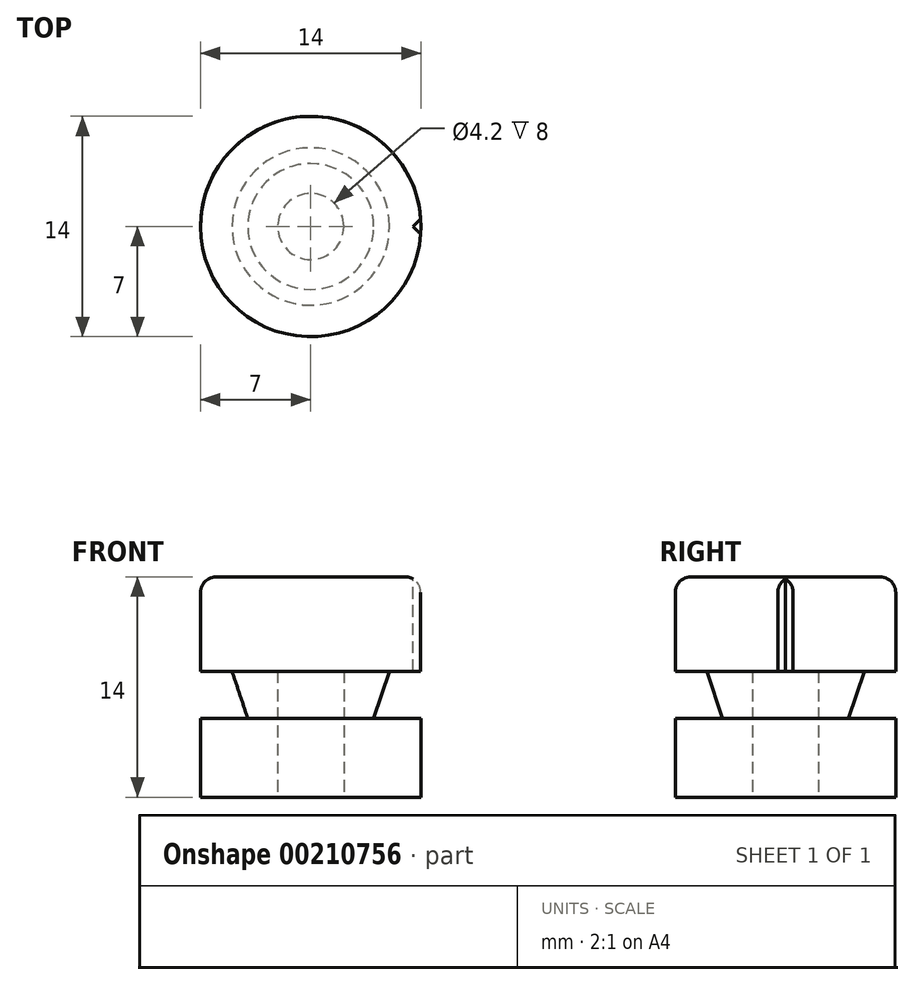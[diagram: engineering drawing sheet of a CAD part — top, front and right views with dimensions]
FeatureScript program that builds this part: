
annotation { "Feature Type Name" : "Feature", "Feature Type Description" : "" }
export const myFeature = defineFeature(function(context is Context, id is Id, definition is map)
    precondition{}
    {
        {
            var Q0;
            Q0=qCreatedBy(makeId("Top.planeOp"),FACE);
            var sketch = newSketch(context, id + "F0", { "sketchPlane" : qUnion([Q0])});
            skCircle(sketch, "E0", {"center": v(0, 0) * mm, "radius": 7 * mm});
            skSolve(sketch);
        }
        {
            var Q0;
            Q0 = qSketchRegion(id + "F0", true);
            extrude(context, id + "F1", {"entities" : qUnion([Q0]), "depth" : 14 * mm});
        }
        {
            var Q0;
            Q0=qCreatedBy(makeId("Front.planeOp"),FACE);
            var sketch = newSketch(context, id + "F2", { "sketchPlane" : qUnion([Q0])});
            skLineSegment(sketch, "E1", {"start": v(7, 8) * mm, "end": v(7, 5) * mm});
            skLineSegment(sketch, "E2", {"start": v(7, 5) * mm, "end": v(4, 5) * mm});
            skLineSegment(sketch, "E3", {"start": v(4, 5) * mm, "end": v(5, 8) * mm});
            skLineSegment(sketch, "E4", {"start": v(5, 8) * mm, "end": v(7, 8) * mm});
            skLineSegment(sketch, "E5", {"start": v(0, 17.83) * mm, "end": v(0, -1.2) * mm, "construction": true});
            skSolve(sketch);
        }
        {
            var Q0;
            Q0 = qSketchRegion(id + "F2", true);
            var Q1;
            Q1=sQuery(id+"F2.wireOp",EDGE,"E5");
            revolve(context, id + "F3", {"operationType" : NewBodyOperationType.REMOVE, "entities" : qUnion([Q0]), "axis" : qUnion([Q1]), "revolveType" : RevolveType.FULL, "oppositeDirection" : true});
        }
        {
            var Q0;
            Q0=makeQuery(id+"F1.opExtrude","CAP_EDGE",EDGE,{"disambiguationData":[OSD([sQuery(id+"F0.wireOp",EDGE,"E0")])],"isStart":false});
            fillet(context, id + "F4", {"entities" : qUnion([Q0]), "radius" : 1 * mm, "tangentPropagation" : true, "allowEdgeOverflow" : false});
        }
        {
            var Q0;
            Q0=makeQuery(id+"F1.opExtrude","CAP_FACE",FACE,{"disambiguationData":[OSD([sQuery(id+"F0.wireOp",EDGE,"E0")])],"isStart":false});
            var sketch = newSketch(context, id + "F5", { "sketchPlane" : qUnion([Q0])});
            skLineSegment(sketch, "E6", {"start": v(0, 0) * mm, "end": v(8.44, 0) * mm, "construction": true});
            skLineSegment(sketch, "E7", {"start": v(6.98, 0.48) * mm, "end": v(6.5, 0) * mm});
            skLineSegment(sketch, "E8", {"start": v(6.5, 0) * mm, "end": v(6.98, -0.48) * mm});
            skArc(sketch, "E9", {"start": v(6.98, -0.48) * mm, "mid": v(7, 0) * mm, "end": v(6.98, 0.48) * mm});
            skSolve(sketch);
        }
        {
            var Q0;
            Q0 = qSketchRegion(id + "F5", true);
            var Q1;
            {var subQ0=sQuery(id+"F5.wireOp",EDGE,"E7");Q1=makeQuery(id+"F5.imprint","IMPRINT",FACE,{"disambiguationData":[TD([[makeQuery(id+"F5.imprint","IMPRINT",EDGE,{"derivedFrom":subQ0}),1.0]])]});}
            var Q2;
            Q2=makeQuery(id+"F3.boolean.opBoolean","COPY",FACE,{"derivedFrom":makeQuery(id+"F3.opRevolve","SWEPT_FACE",FACE,{"disambiguationData":[OSD([sQuery(id+"F2.wireOp",EDGE,"E4")])]})});
            extrude(context, id + "F6", {"entities" : qUnion([Q0, Q1]), "operationType" : NewBodyOperationType.REMOVE, "endBound" : BoundingType.UP_TO_SURFACE, "oppositeDirection" : true, "endBoundEntityFace" : qUnion([Q2]), "depth" : 25 * mm});
        }
        {
            var Q0;
            Q0=makeQuery(id+"F1.opExtrude","CAP_FACE",FACE,{"disambiguationData":[OSD([sQuery(id+"F0.wireOp",EDGE,"E0")])],"isStart":true});
            var sketch = newSketch(context, id + "F7", { "sketchPlane" : qUnion([Q0])});
            skCircle(sketch, "E10", {"center": v(0, 0) * mm, "radius": 2.1 * mm});
            skSolve(sketch);
        }
        {
            var Q0;
            Q0 = qSketchRegion(id + "F7", true);
            extrude(context, id + "F8", {"entities" : qUnion([Q0]), "operationType" : NewBodyOperationType.REMOVE, "oppositeDirection" : true, "depth" : 8 * mm});
        }
    });
